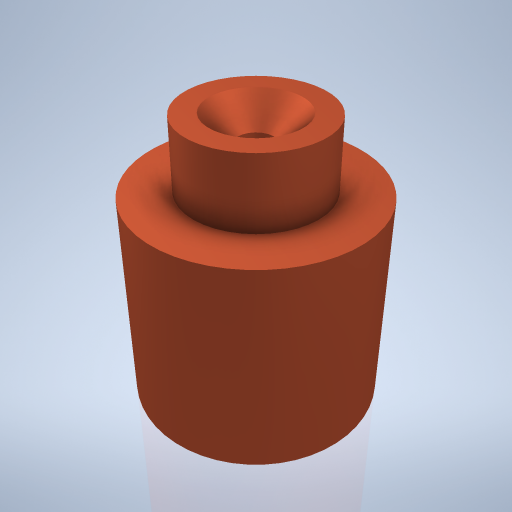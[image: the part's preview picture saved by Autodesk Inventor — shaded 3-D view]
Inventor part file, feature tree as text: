
AUTODESK INVENTOR PART (.ipt)
format: ipt  version: 2024.2 (Build 282272000, 272)  size: 254,976 bytes
history: native  units: mm
features: sketch x4, extrude x2, hole x2
ambient origin geometry x8: Origin, YZ Plane, XZ Plane, XY Plane, X Axis, Y Axis, Z Axis, Center Point
bodies: Volumenkörper1 (feature_tree)
feature tree (8):
  extrude  "Extrusion1"  Depth=9.0mm TaperAngle=0.0deg
  extrude  "Extrusion2"  Depth=3.0mm TaperAngle=0.0deg
  hole  "Bohrung1"  [1 undecoded]
  hole  "Bohrung2"  [1 undecoded]
  sketch  "Skizze1"  dims[d0=10.0mm d1=9.0mm d2=0.0mm]
  sketch  "Skizze2"  dims[d3=6.0mm d4=3.0mm d5=0.0mm]
  sketch  "Skizze3"  dims[d6=1.6mm d7=6.0mm d8=4.0mm d9=2.0mm d10=90.0deg d11=6.0mm d12=0.0mm]
  sketch  "Skizze4"  dims[d13=1.6mm d14=6.0mm d15=4.0mm d16=2.0mm d17=90.0deg d18=6.0mm d19=0.0mm]
note: 2 required parameter values undecoded (feature->parameter linkage not recoverable at this tier; creation-order binding heuristic only, values carry confidence <= 0.55)
